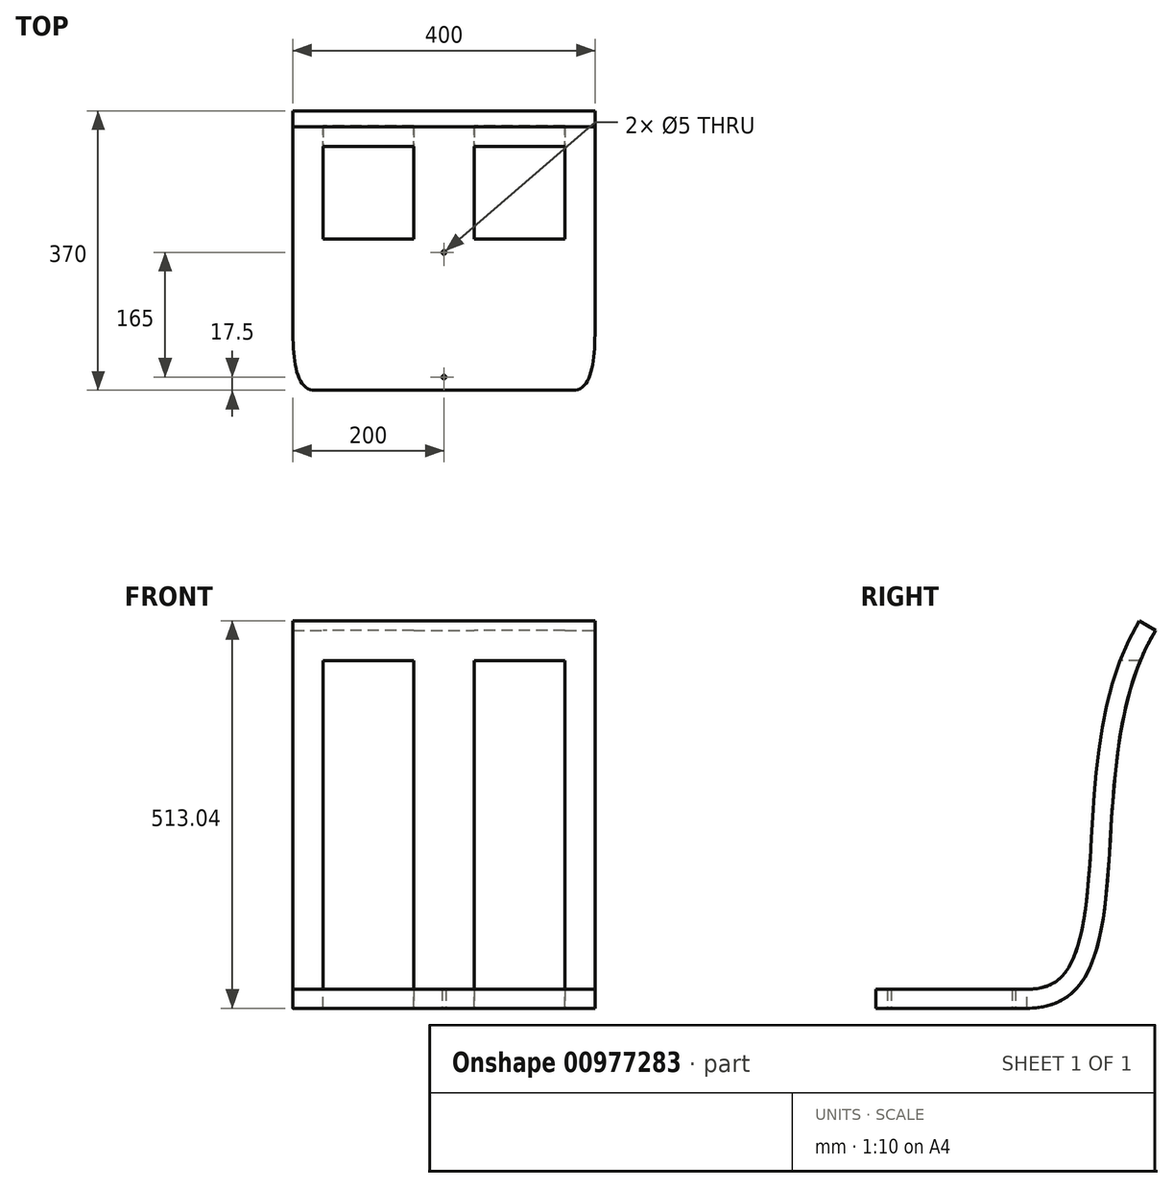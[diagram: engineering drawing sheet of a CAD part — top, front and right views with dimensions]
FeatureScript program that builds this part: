
annotation { "Feature Type Name" : "Feature", "Feature Type Description" : "" }
export const myFeature = defineFeature(function(context is Context, id is Id, definition is map)
    precondition{}
    {
        {
            var Q0;
            Q0=qCreatedBy(makeId("Top.planeOp"),FACE);
            var sketch = newSketch(context, id + "F0", { "sketchPlane" : qUnion([Q0])});
            skLineSegment(sketch, "E0.bottom", {"start": v(-200, 100) * mm, "end": v(200, 100) * mm});
            skLineSegment(sketch, "E0.top", {"start": v(-200, -100) * mm, "end": v(200, -100) * mm});
            skLineSegment(sketch, "E0.left", {"start": v(-200, 100) * mm, "end": v(-200, -100) * mm});
            skLineSegment(sketch, "E0.right", {"start": v(200, 100) * mm, "end": v(200, -100) * mm});
            skPoint(sketch, "E0.middle", {"position": v(0, 0) * mm});
            skFitSpline(sketch, "E1", {"points": [v(170, 100) * mm, v(200, 0) * mm, v(170, -100) * mm], "startDerivative": vector(180, 0) * mm, "endDerivative": vector(-180, 0) * mm});
            skFitSpline(sketch, "E2", {"points": [v(-170, -100) * mm, v(-200, 0) * mm, v(-170, 100) * mm], "startDerivative": vector(-180, 0) * mm, "endDerivative": vector(180, 0) * mm});
            skPoint(sketch, "E3", {"position": v(0, -82.5) * mm});
            skPoint(sketch, "E4", {"position": v(0, 82.5) * mm});
            skSolve(sketch);
        }
        {
            var Q0;
            {var subQ0=sQuery(id+"F0.wireOp",EDGE,"E1");var subQ1=sQuery(id+"F0.wireOp",EDGE,"E0.bottom");var subQ2=makeQuery(id+"F0.imprint","INTERSECT",VERTEX,{"derivedFrom":[subQ1,subQ0]});Q0=makeQuery(id+"F0.imprint","IMPRINT",FACE,{"disambiguationData":[TD([[makeQuery(id+"F0.imprint","IMPRINT",EDGE,{"disambiguationData":[TD([[subQ2,1.0]])],"derivedFrom":subQ1}),-1.0]])]});}
            var Q1;
            {var subQ0=sQuery(id+"F0.wireOp",EDGE,"E0.right");var subQ1=sQuery(id+"F0.wireOp",EDGE,"E0.bottom");var subQ2=makeQuery(id+"F0.imprint","INTERSECT",VERTEX,{"derivedFrom":[subQ1,subQ0]});Q1=makeQuery(id+"F0.imprint","IMPRINT",FACE,{"disambiguationData":[TD([[makeQuery(id+"F0.imprint","IMPRINT",EDGE,{"disambiguationData":[TD([[subQ2,1.0]])],"derivedFrom":subQ1}),-1.0]])]});}
            var Q2;
            {var subQ0=sQuery(id+"F0.wireOp",EDGE,"E0.left");var subQ1=sQuery(id+"F0.wireOp",EDGE,"E0.bottom");var subQ2=makeQuery(id+"F0.imprint","INTERSECT",VERTEX,{"derivedFrom":[subQ1,subQ0]});Q2=makeQuery(id+"F0.imprint","IMPRINT",FACE,{"disambiguationData":[TD([[makeQuery(id+"F0.imprint","IMPRINT",EDGE,{"disambiguationData":[TD([[subQ2,-1.0]])],"derivedFrom":subQ1}),-1.0]])]});}
            extrude(context, id + "F1", {"entities" : qUnion([Q0, Q1, Q2]), "depth" : 25 * mm, "offsetDistance" : 25 * mm});
        }
        {
            var Q0;
            Q0=qCreatedBy(makeId("Right.planeOp"),FACE);
            var sketch = newSketch(context, id + "F2", { "sketchPlane" : qUnion([Q0])});
            skFitSpline(sketch, "E5", {"points": [v(100, 0) * mm, v(270, 500) * mm], "startDerivative": vector(510, 0) * mm, "endDerivative": vector(330, 540) * mm});
            skSolve(sketch);
        }
        {
            var Q0;
            Q0=makeQuery(id+"F1.opExtrude","SWEPT_FACE",FACE,{"disambiguationData":[OSD([sQuery(id+"F0.wireOp",EDGE,"E0.bottom")])]});
            var sketch = newSketch(context, id + "F3", { "sketchPlane" : qUnion([Q0])});
            skLineSegment(sketch, "E6.bottom", {"start": v(-200, 25) * mm, "end": v(-160, 25) * mm});
            skLineSegment(sketch, "E6.top", {"start": v(-200, 0) * mm, "end": v(-160, 0) * mm});
            skLineSegment(sketch, "E6.left", {"start": v(-200, 25) * mm, "end": v(-200, 0) * mm});
            skLineSegment(sketch, "E6.right", {"start": v(-160, 25) * mm, "end": v(-160, 0) * mm});
            skLineSegment(sketch, "E7.bottom", {"start": v(200, 0) * mm, "end": v(160, 0) * mm});
            skLineSegment(sketch, "E7.top", {"start": v(200, 25) * mm, "end": v(160, 25) * mm});
            skLineSegment(sketch, "E7.left", {"start": v(200, 0) * mm, "end": v(200, 25) * mm});
            skLineSegment(sketch, "E7.right", {"start": v(160, 0) * mm, "end": v(160, 25) * mm});
            skLineSegment(sketch, "E8.bottom", {"start": v(40, 25) * mm, "end": v(-40, 25) * mm});
            skLineSegment(sketch, "E8.top", {"start": v(40, 0) * mm, "end": v(-40, 0) * mm});
            skLineSegment(sketch, "E8.left", {"start": v(40, 25) * mm, "end": v(40, 0) * mm});
            skLineSegment(sketch, "E8.right", {"start": v(-40, 25) * mm, "end": v(-40, 0) * mm});
            skSolve(sketch);
        }
        {
            var Q0;
            Q0=makeQuery(id+"F3.imprint","IMPRINT",FACE,{"disambiguationData":[TD([[makeQuery(id+"F3.imprint","IMPRINT",EDGE,{"derivedFrom":sQuery(id+"F3.wireOp",EDGE,"E6.bottom")}),1.0]])]});
            var Q1;
            Q1=makeQuery(id+"F3.imprint","IMPRINT",FACE,{"disambiguationData":[TD([[makeQuery(id+"F3.imprint","IMPRINT",EDGE,{"derivedFrom":sQuery(id+"F3.wireOp",EDGE,"E8.bottom")}),1.0]])]});
            var Q2;
            Q2=makeQuery(id+"F3.imprint","IMPRINT",FACE,{"disambiguationData":[TD([[makeQuery(id+"F3.imprint","IMPRINT",EDGE,{"derivedFrom":sQuery(id+"F3.wireOp",EDGE,"E7.bottom")}),-1.0]])]});
            var Q3;
            Q3=sQuery(id+"F2.wireOp",EDGE,"E5");
            sweep(context, id + "F4", {"operationType" : NewBodyOperationType.ADD, "profiles" : qUnion([Q0, Q1, Q2]), "path" : qUnion([Q3])});
        }
        {
            var Q0;
            Q0=sQuery(id+"F0.wireOp",VERTEX,"E3");
            var Q1;
            Q1=sQuery(id+"F0.wireOp",VERTEX,"E4");
            var Q2;
            Q2=makeQuery(id+"F1.opExtrude","SWEPT_BODY",BODY,{"disambiguationData":[OSD([sQuery(id+"F0.wireOp",EDGE,"E0.bottom"),sQuery(id+"F0.wireOp",EDGE,"E0.top"),sQuery(id+"F0.wireOp",EDGE,"E0.left"),sQuery(id+"F0.wireOp",EDGE,"E0.right"),sQuery(id+"F0.wireOp",EDGE,"E1"),sQuery(id+"F0.wireOp",EDGE,"E2")])]});
            hole(context, id + "F5", {"style" : HoleStyle.SIMPLE, "endStyle" : HoleEndStyle.BLIND, "oppositeDirection" : true, "holeDiameter" : 5 * mm, "majorDiameter" : 5 * mm, "holeDepth" : 25 * mm, "isTappedThrough" : true, "tappedDepth" : 12 * mm, "tapClearance" : 3, "locations" : qUnion([Q0, Q1]), "scope" : qUnion([Q2])});
        }
        {
            var Q0;
            Q0=makeQuery(id+"F4.opSweep","SWEPT_FACE",FACE,{"disambiguationData":[OSD([sQuery(id+"F2.wireOp",EDGE,"E5"),sQuery(id+"F3.wireOp",EDGE,"E7.right")])]});
            var sketch = newSketch(context, id + "F6", { "sketchPlane" : qUnion([Q0])});
            skLineSegment(sketch, "E9", {"start": v(249.84, 460) * mm, "end": v(222.95, 460) * mm});
            skSolve(sketch);
        }
        {
            var Q0;
            {var subQ0=sQuery(id+"F6.wireOp",EDGE,"E9");Q0=makeQuery(id+"F6.imprint","IMPRINT",FACE,{"disambiguationData":[TD([[makeQuery(id+"F6.imprint","IMPRINT",EDGE,{"derivedFrom":subQ0}),-1.0]])]});}
            extrude(context, id + "F7", {"entities" : qUnion([Q0]), "operationType" : NewBodyOperationType.ADD, "depth" : 350 * mm, "offsetDistance" : 25 * mm});
        }
    });
